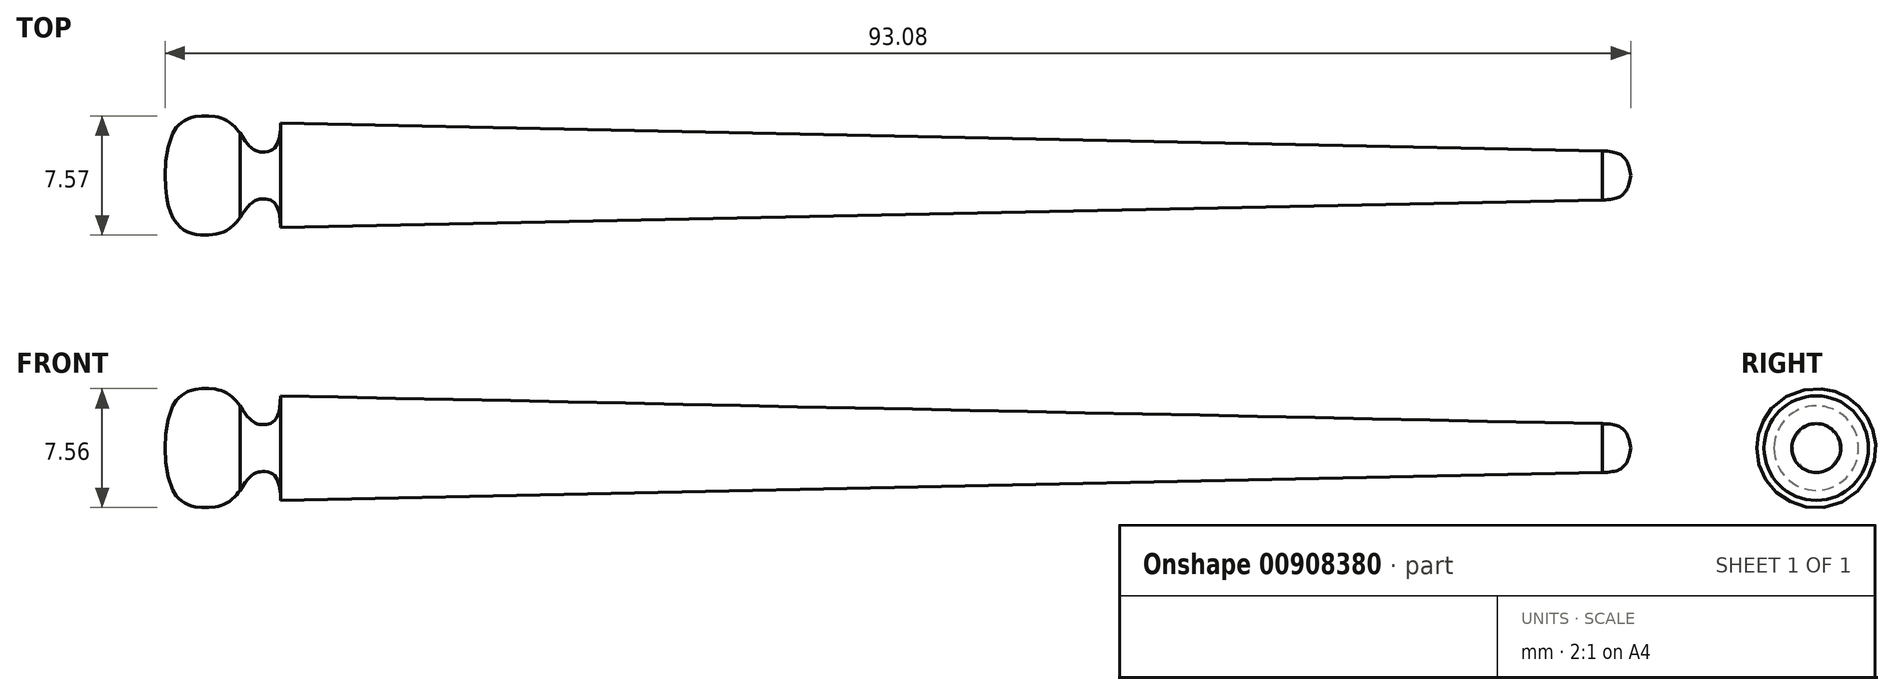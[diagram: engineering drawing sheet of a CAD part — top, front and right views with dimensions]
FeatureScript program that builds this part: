
annotation { "Feature Type Name" : "Feature", "Feature Type Description" : "" }
export const myFeature = defineFeature(function(context is Context, id is Id, definition is map)
    precondition{}
    {
        {
            var Q0;
            Q0=qCreatedBy(makeId("Top.planeOp"),FACE);
            var sketch = newSketch(context, id + "F0", { "sketchPlane" : qUnion([Q0])});
            skLineSegment(sketch, "E0", {"start": v(-46.65, 17.45) * mm, "end": v(46.43, 17.45) * mm});
            skLineSegment(sketch, "E1", {"start": v(44.63, 15.9) * mm, "end": v(-39.32, 14.13) * mm});
            skFitSpline(sketch, "E2", {"points": [v(-46.65, 17.45) * mm, v(-44.06, 13.67) * mm, v(-41.9, 14.76) * mm], "startDerivative": vector(0, -18.02) * mm, "endDerivative": vector(4.68, 6.53) * mm});
            skFitSpline(sketch, "E3", {"points": [v(-41.9, 14.76) * mm, v(-40.43, 15.95) * mm, v(-39.32, 14.13) * mm], "startDerivative": vector(3.98, 6.51) * mm, "endDerivative": vector(0, -10.06) * mm});
            skFitSpline(sketch, "E4", {"points": [v(46.43, 17.45) * mm, v(45.97, 16.27) * mm, v(44.63, 15.9) * mm], "startDerivative": vector(-0.47, -3.76) * mm, "endDerivative": vector(-4.5, -0.16) * mm});
            skSolve(sketch);
        }
        {
            var Q0;
            Q0=makeQuery(id+"F0.imprint","IMPRINT",FACE,{"disambiguationData":[TD([[makeQuery(id+"F0.imprint","IMPRINT",EDGE,{"derivedFrom":sQuery(id+"F0.wireOp",EDGE,"E0")}),-1.0]])]});
            var Q1;
            Q1=sQuery(id+"F0.wireOp",EDGE,"E0");
            revolve(context, id + "F1", {"surfaceOperationType" : NewSurfaceOperationType.NEW, "entities" : qUnion([Q0]), "axis" : qUnion([Q1]), "revolveType" : RevolveType.FULL});
        }
    });
